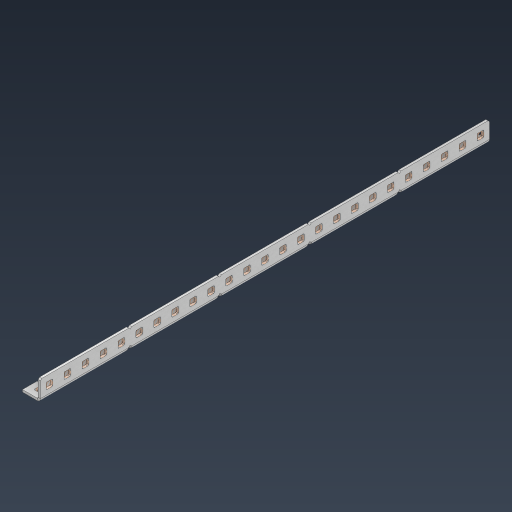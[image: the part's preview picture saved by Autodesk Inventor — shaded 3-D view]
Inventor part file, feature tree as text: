
AUTODESK INVENTOR PART (.ipt)
format: ipt  version: 2024.3 (Build 283343000, 343)  size: 986,112 bytes
history: native  units: in
note: dims shown in document units (in); Inventor stores cm internally (conversion verified against a paired STEP export)
features: other x82, extrude x73, sheet_metal_op x11, pattern_linear x2, mirror x1, chamfer x1, sketch x1
ambient origin geometry x8: Origin, YZ Plane, XZ Plane, XY Plane, X Axis, Y Axis, Z Axis, Center Point
bodies: Solid1 (feature_tree), Body (feature_tree)
feature tree (171):
  sheet_metal_op  "Flanges"
  other  "Flange Pattern Plane"
  other  "Flange Pattern Sketch"
  sheet_metal_op  "Flange Pattern"
  sheet_metal_op  "Body Pattern"
  pattern_linear  "Center Pattern"  Spacing1=12.5in  [1 undecoded]
  other  "Arc Length"
  mirror  "Notch Mirror"
  pattern_linear  "Notch Pattern"  Spacing1=0.0625in  [1 undecoded]
  chamfer  "End Chamfer"
  extrude  "Half Cut"  Depth=0.0625in
  other  "Plate1"
  sketch  "Sketch2"  dims[d0=1.0in d1=12.5in d2=0.0625in d3=0.0625in d4=0.0312in d5=0.125in d6=0.0625in d7=0.5in d8=90.0deg d9=0.0312in d10=0.25in d11=0.0625in d12=0.0625in d16=0.182in d17=0.02in d18=0.0625in d19=0.0in d20=0.25in d21=0.25in d38=9.8425in d40=0.5in d41=0.3937in d43=1.0in d46=0.172in d47=1.0in d48=0.0in d49=0.182in d50=0.02in d51=0.25in d52=0.25in d53=0.0625in d54=0.0in d55=0.172in d56=1.0in d57=0.0in d58=0.25in d60=9.8425in d62=0.5in d63=0.3937in d65=0.5in d85=0.1473in d86=0.1782in d88=0.04in d89=0.0625in d90=0.0in d91=0.04in d92=0.0491in d95=2.5in d96=0.04in d97=0.25in d98=45.0deg d99=0.25in d100=0.5in d101=0.0in d102=2.497in d106=0.182in d107=0.02in d108=0.5in d109=0.5in d110=0.0625in d111=0.0in d112=0.172in d113=0.5in d114=0.0in d117=0.5in d118=0.5in d119=0.5in]
  other  "Plate2"
  sheet_metal_op  "Bend1"
  sheet_metal_op  "Corner1"
  other  "Srf1"
  other  "Srf2"
  other  "Srf91"
  sheet_metal_op  "Body Pattern Sketch"
  other  "Srf92"
  other  "Srf786"
  other  "Srf823"
  other  "Srf824"
  other  "Srf825"
  other  "Srf826"
  other  "Srf827"
  other  "Srf828"
  other  "Srf829"
  other  "Srf856"
  other  "Srf857"
  other  "Srf858"
  other  "Srf859"
  other  "Srf860"
  other  "Srf861"
  other  "Srf862"
  other  "Srf889"
  other  "Srf890"
  other  "Srf891"
  other  "Srf892"
  other  "Srf893"
  other  "Srf894"
  other  "Srf895"
  other  "Srf896"
  other  "Srf922"
  other  "Srf923"
  other  "Srf924"
  other  "Srf925"
  other  "Srf926"
  other  "Srf959"
  other  "Srf960"
  other  "Srf961"
  other  "Srf962"
  other  "Srf963"
  other  "Srf996"
  other  "Srf997"
  other  "Srf998"
  other  "Srf999"
  other  "Srf1000"
  other  "Srf1143"
  other  "Srf1144"
  other  "Srf1145"
  other  "Srf1146"
  other  "Srf1147"
  other  "Srf1148"
  other  "Srf1149"
  other  "Srf1150"
  other  "Srf1151"
  other  "Srf1152"
  other  "Srf1153"
  other  "Srf1199"
  other  "Srf1200"
  other  "Srf1201"
  other  "Srf1202"
  other  "Srf1203"
  other  "Srf1204"
  other  "Srf1205"
  other  "Srf1206"
  other  "Srf1207"
  other  "Srf1208"
  other  "Srf1209"
  other  "Srf1255"
  other  "Srf1256"
  other  "Srf1257"
  other  "Srf1258"
  other  "Srf1259"
  other  "Srf1260"
  other  "Srf1261"
  other  "Srf1262"
  other  "Srf1263"
  other  "Srf1264"
  other  "Srf1265"
  sheet_metal_op  "Flange Stamp"
  sheet_metal_op  "Flange Circle"
  sheet_metal_op  "Body Stamp"
  sheet_metal_op  "Body Circle"
  other  "Center Stamp"
  other  "Center Circle"
  sheet_metal_op  "Notch"
  extrude  "ExtrusionSrf2"  Depth=0.0312in
  extrude  "ExtrusionSrf92"  Depth=0.5in
  extrude  "ExtrusionSrf823"  Depth=0.0625in
  extrude  "ExtrusionSrf824"  Depth=0.5in TaperAngle=90.0deg
  extrude  "ExtrusionSrf825"  Depth=0.5in
  extrude  "ExtrusionSrf826"  Depth=0.0625in
  extrude  "ExtrusionSrf827"  Depth=0.0625in
  extrude  "ExtrusionSrf828"  Depth=0.182in
  extrude  "ExtrusionSrf829"  Depth=0.02in
  extrude  "ExtrusionSrf856"  Depth=0.0625in
  extrude  "ExtrusionSrf857"  TaperAngle=0.0deg  [1 undecoded]
  extrude  "ExtrusionSrf858"  Depth=0.5in
  extrude  "ExtrusionSrf859"  Depth=0.5in
  extrude  "ExtrusionSrf860"  Depth=0.5in
  extrude  "ExtrusionSrf861"  Depth=0.5in
  extrude  "ExtrusionSrf862"  Depth=1.0in TaperAngle=0.0deg
  extrude  "ExtrusionSrf889"  Depth=0.182in
  extrude  "ExtrusionSrf890"  Depth=0.02in
  extrude  "ExtrusionSrf891"  Depth=0.5in
  extrude  "ExtrusionSrf892"  Depth=0.5in
  extrude  "ExtrusionSrf893"  Depth=0.0625in
  extrude  "ExtrusionSrf894"  TaperAngle=0.0deg  [1 undecoded]
  extrude  "ExtrusionSrf895"  Depth=0.5in
  extrude  "ExtrusionSrf896"  Depth=1.0in TaperAngle=0.0deg
  extrude  "ExtrusionSrf922"  Depth=0.5in
  extrude  "ExtrusionSrf923"  Depth=0.5in
  extrude  "ExtrusionSrf924"  Depth=0.5in
  extrude  "ExtrusionSrf925"  Depth=0.5in
  extrude  "ExtrusionSrf926"  Depth=0.5in
  extrude  "ExtrusionSrf959"  Depth=0.5in
  extrude  "ExtrusionSrf960"  Depth=0.0625in
  extrude  "ExtrusionSrf961"  TaperAngle=0.0deg  [1 undecoded]
  extrude  "ExtrusionSrf962"  Depth=0.5in
  extrude  "ExtrusionSrf963"  Depth=0.5in
  extrude  "ExtrusionSrf996"  Depth=0.5in
  extrude  "ExtrusionSrf997"  Depth=0.5in TaperAngle=45.0deg
  extrude  "ExtrusionSrf998"  Depth=0.5in
  extrude  "ExtrusionSrf999"  Depth=0.5in TaperAngle=0.0deg
  extrude  "ExtrusionSrf1000"  Depth=0.5in
  extrude  "ExtrusionSrf1143"  Depth=0.182in
  extrude  "ExtrusionSrf1144"  Depth=0.02in
  extrude  "ExtrusionSrf1145"  Depth=0.5in
  extrude  "ExtrusionSrf1146"  Depth=0.5in
  extrude  "ExtrusionSrf1147"  Depth=0.0625in
  extrude  "ExtrusionSrf1148"  TaperAngle=0.0deg  [1 undecoded]
  extrude  "ExtrusionSrf1149"  Depth=0.5in
  extrude  "ExtrusionSrf1150"  Depth=0.5in TaperAngle=0.0deg
  extrude  "ExtrusionSrf1151"  Depth=0.5in
  extrude  "ExtrusionSrf1152"  Depth=0.5in
  extrude  "ExtrusionSrf1153"  Depth=0.5in
  extrude  "ExtrusionSrf1199"  [1 undecoded]
  extrude  "ExtrusionSrf1200"  [1 undecoded]
  extrude  "ExtrusionSrf1201"  [1 undecoded]
  extrude  "ExtrusionSrf1202"  [1 undecoded]
  extrude  "ExtrusionSrf1203"  [1 undecoded]
  extrude  "ExtrusionSrf1204"  [1 undecoded]
  extrude  "ExtrusionSrf1205"  [1 undecoded]
  extrude  "ExtrusionSrf1206"  [1 undecoded]
  extrude  "ExtrusionSrf1207"  [1 undecoded]
  extrude  "ExtrusionSrf1208"  [1 undecoded]
  extrude  "ExtrusionSrf1209"  [1 undecoded]
  extrude  "ExtrusionSrf1255"  [1 undecoded]
  extrude  "ExtrusionSrf1256"  [1 undecoded]
  extrude  "ExtrusionSrf1257"  [1 undecoded]
  extrude  "ExtrusionSrf1258"  [1 undecoded]
  extrude  "ExtrusionSrf1259"  [1 undecoded]
  extrude  "ExtrusionSrf1260"  [1 undecoded]
  extrude  "ExtrusionSrf1261"  [1 undecoded]
  extrude  "ExtrusionSrf1262"  [1 undecoded]
  extrude  "ExtrusionSrf1263"  [1 undecoded]
  extrude  "ExtrusionSrf1264"  [1 undecoded]
  extrude  "ExtrusionSrf1265"  [1 undecoded]
note: 28 required parameter values undecoded (feature->parameter linkage not recoverable at this tier; creation-order binding heuristic only, values carry confidence <= 0.55)
